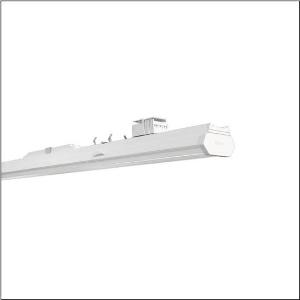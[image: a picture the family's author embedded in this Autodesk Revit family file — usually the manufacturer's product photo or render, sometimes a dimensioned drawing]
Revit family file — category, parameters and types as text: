
# Revit family: licross_11_protected_extreme_mo_51tp12dn49xge
name_source: partatom
category: Lighting Fixtures
units: mm (PartAtom-declared; Revit-internal decimal feet)

## family parameters
Cut with Voids When Loaded = No
Host = Face
Light Source = No
Part Type = Normal
Room Calculation Point = No
Round Connector Dimension = Use Diameter
Shared = No

## types (1)
- --- (1 x LED, 9020 lm, 51 W, 4000K)
    Apparent Load = 51 VA
    CIE Flux Codes = 73 92 98 99 100
    Color Rendering = 80
    Color Temperature = 4000K
    Default Elevation = 1800 mm
    Description = Licross 11 Protected extreme MO, luminaire insert, of sheet steel, galvanised, coil coated, white, length: 1.500mm, width: 90mm, height: 101mm, LED rated luminous flux: 9.020lm, light colour: 840, SDCM (Standard Deviation of Colour Matching)MacAdam ≤ 2 SDCM (initial), control gear: DALI 2, with plug, 5-pole, with phase selection, mains connection: 220..240V, AC, 50/60Hz, rated input power: 51W, internal wiring halogen-free, primary optical cover: cover, of PMMA, light emission: direct distribution, primary light characteristic: symmetric, protection rating (complete): IP64, insulation class (complete): insulation class I (protective earthing), certification: CE, ENEC, VDE, UKCA, protection symbol: D if used in an environment with conductive dust loads with corresponding accessories, impact resistance: IK06, permissible ambient temperature for indoor applications: -40..+50°C, LABS conformity tested according to VDMA 24364:2018-05, reducing of maximum allowable ambient temperature of 5°C with ceiling mounting, corresponds to IFS (International Featured Standards) requirements for safety and quality in the food industry, The light source and the operating device comply with the requirements of the Ecodesign Regulation (EU) 2019/2020 and are replaceable in accordance with this regulation, packaging unit: 1 piece
    Height = 92 mm
    Lamp = 1 x LED
    Lamp Light Flux = 9020 lm
    Lamp Power = 51 W
    Lamp count = 1
    Length = 1500 mm
    Luminous efficacy = 177 lm/W
    Manufacturer = Siteco
    ModVariant = No
    Model = 51TP12DN49XGE
    Mounting Place = Ceiling
    Mounting Type = Pendant
    Number of Poles = 1
    OnlyDefault = Yes
    Power Factor = 1
    Product Name = Licross 11 Protected extreme MO
    Product group = luminaire insert | ceiling pendant
    ProductGroupID = 901
    Protection Class = Protection class I
    Protection Degree = IP 64
    RLX_Detail_Level = 1
    RLX_Emergency_Light_Flux = 0 lm
    RLX_Emergency_Type = 0
    RLX_Emergency_Type_DB = No
    RlxData = <blob elided: 24757 chars, md5=5c96a2ea>
    Socket = socket
    Standby Power = 0 W
    System Light Flux = 9020 lm
    System Power = 51 W
    Type Comments = factory setting: luminous flux: 100 % | dim-lin: 254 | 339 mA
    Type Image = l_1256148.jpg
    URL = http://relux.com
    VarID = @adj_021101
    Voltage = 0 V
    Weight = 0.00 kg
    Width = 88 mm

## geometry (parser evidence)
native form markers: Blend x4, Sweep x10
no freeform markers — native parametric forms only
